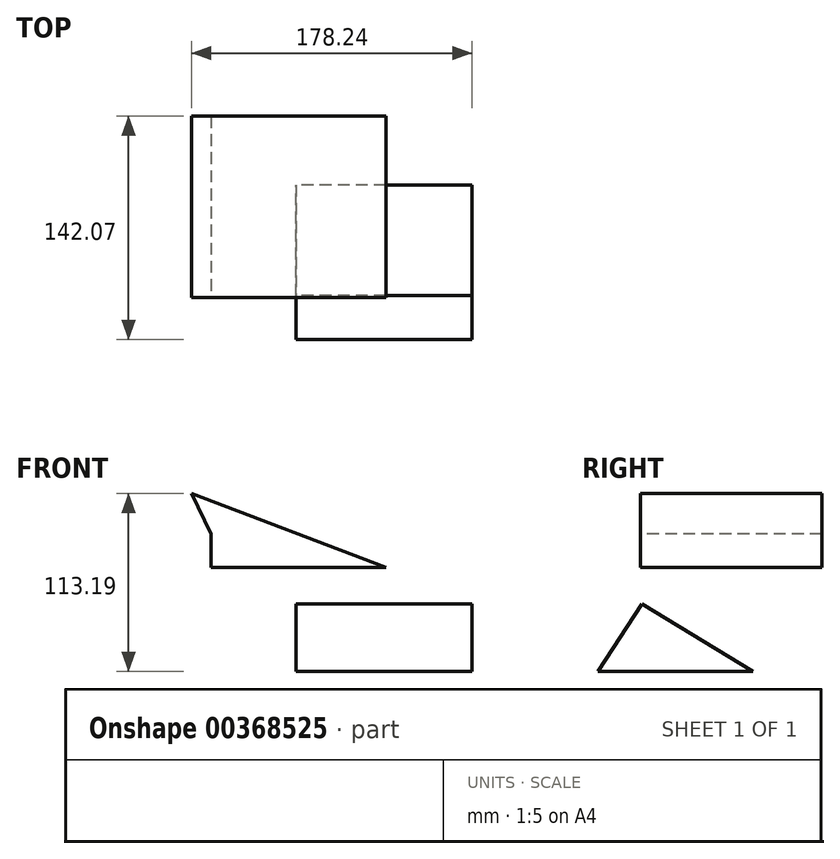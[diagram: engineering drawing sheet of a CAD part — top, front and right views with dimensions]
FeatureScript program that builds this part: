
annotation { "Feature Type Name" : "Feature", "Feature Type Description" : "" }
export const myFeature = defineFeature(function(context is Context, id is Id, definition is map)
    precondition{}
    {
        {
            var Q0;
            Q0=qCreatedBy(makeId("Front.planeOp"),FACE);
            var sketch = newSketch(context, id + "F0", { "sketchPlane" : qUnion([Q0])});
            skLineSegment(sketch, "E0", {"start": v(-54, 36.87) * mm, "end": v(56.92, 36.87) * mm});
            skLineSegment(sketch, "E1", {"start": v(56.92, 36.87) * mm, "end": v(56.92, -36.14) * mm});
            skLineSegment(sketch, "E2", {"start": v(56.92, -36.14) * mm, "end": v(-54, -33.83) * mm});
            skLineSegment(sketch, "E3", {"start": v(-54, -33.83) * mm, "end": v(-54, 58.3) * mm});
            skLineSegment(sketch, "E4", {"start": v(-54, 58.3) * mm, "end": v(-66.45, 84.13) * mm});
            skLineSegment(sketch, "E5", {"start": v(-66.45, 84.13) * mm, "end": v(56.92, 36.87) * mm});
            skLineSegment(sketch, "E6", {"start": v(-54, -33.83) * mm, "end": v(-66.45, 84.13) * mm});
            skSolve(sketch);
        }
        {
            var Q0;
            Q0=qCreatedBy(makeId("Right.planeOp"),FACE);
            var sketch = newSketch(context, id + "F1", { "sketchPlane" : qUnion([Q0])});
            skLineSegment(sketch, "E7", {"start": v(71.51, 32.36) * mm, "end": v(-29.75, 32.36) * mm});
            skLineSegment(sketch, "E8", {"start": v(-29.75, 32.36) * mm, "end": v(71.51, -29.06) * mm});
            skLineSegment(sketch, "E9", {"start": v(71.51, -29.06) * mm, "end": v(-26.89, -29.06) * mm});
            skLineSegment(sketch, "E10", {"start": v(-26.89, -29.06) * mm, "end": v(12.96, 31.91) * mm});
            skSolve(sketch);
        }
        {
            var Q0;
            {var subQ0=sQuery(id+"F0.wireOp",EDGE,"E0");Q0=makeQuery(id+"F0.imprint","IMPRINT",FACE,{"disambiguationData":[TD([[makeQuery(id+"F0.imprint","IMPRINT",EDGE,{"derivedFrom":subQ0}),1.0]])]});}
            extrude(context, id + "F2", {"entities" : qUnion([Q0]), "oppositeDirection" : true, "depth" : 115.18 * mm});
        }
        {
            var Q0;
            {var subQ0=sQuery(id+"F1.wireOp",EDGE,"E9");Q0=makeQuery(id+"F1.imprint","IMPRINT",FACE,{"disambiguationData":[TD([[makeQuery(id+"F1.imprint","IMPRINT",EDGE,{"derivedFrom":subQ0}),-1.0]])]});}
            extrude(context, id + "F3", {"entities" : qUnion([Q0]), "depth" : 111.8 * mm});
        }
    });
